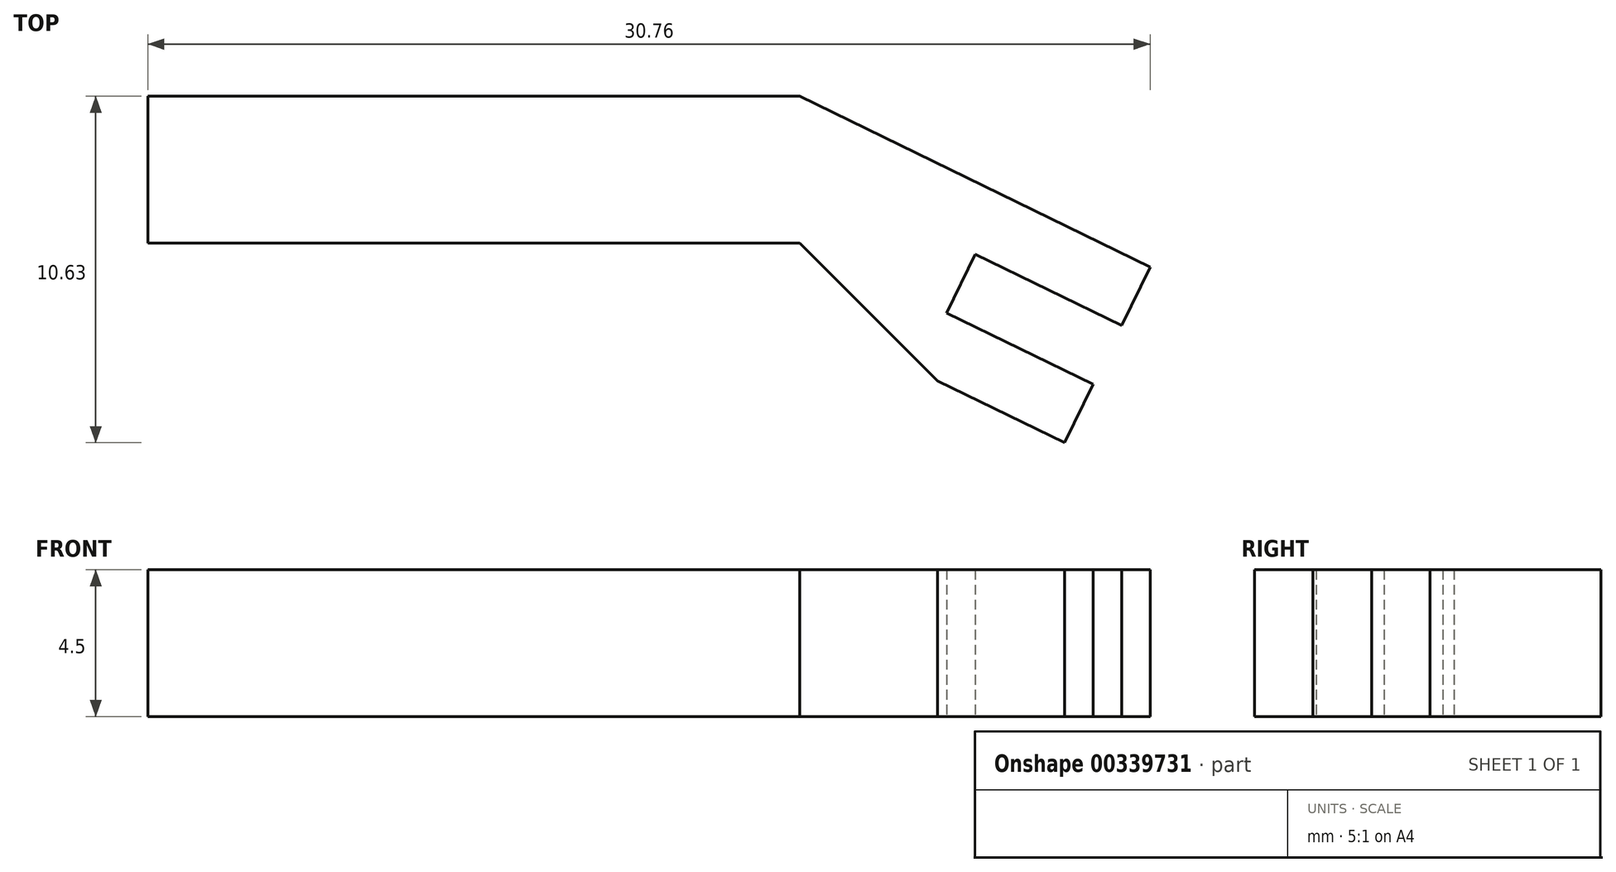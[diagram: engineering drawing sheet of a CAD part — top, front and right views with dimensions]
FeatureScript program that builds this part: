
annotation { "Feature Type Name" : "Feature", "Feature Type Description" : "" }
export const myFeature = defineFeature(function(context is Context, id is Id, definition is map)
    precondition{}
    {
        {
            var Q0;
            Q0=qCreatedBy(makeId("Top.planeOp"),FACE);
            var sketch = newSketch(context, id + "F0", { "sketchPlane" : qUnion([Q0])});
            skLineSegment(sketch, "E0.bottom", {"start": v(10, -2.25) * mm, "end": v(-10, -2.25) * mm});
            skLineSegment(sketch, "E0.top", {"start": v(10, 2.25) * mm, "end": v(-10, 2.25) * mm});
            skLineSegment(sketch, "E0.left", {"start": v(10, -2.25) * mm, "end": v(10, 2.25) * mm});
            skLineSegment(sketch, "E0.right", {"start": v(-10, -2.25) * mm, "end": v(-10, 2.25) * mm});
            skPoint(sketch, "E0.middle", {"position": v(0, 0) * mm});
            skLineSegment(sketch, "E1", {"start": v(10, 2.25) * mm, "end": v(20.76, -2.99) * mm});
            skLineSegment(sketch, "E2", {"start": v(20.76, -2.99) * mm, "end": v(17.48, -9.73) * mm});
            skLineSegment(sketch, "E3", {"start": v(17.48, -9.73) * mm, "end": v(10, -2.25) * mm});
            skPoint(sketch, "E4", {"position": v(19.12, -6.36) * mm});
            skLineSegment(sketch, "E5", {"start": v(19.01, -6.58) * mm, "end": v(14.52, -4.4) * mm});
            skLineSegment(sketch, "E6", {"start": v(14.52, -4.4) * mm, "end": v(15.4, -2.6) * mm});
            skLineSegment(sketch, "E7", {"start": v(15.4, -2.6) * mm, "end": v(19.89, -4.79) * mm});
            skPoint(sketch, "E8", {"position": v(18.14, -8.38) * mm});
            skLineSegment(sketch, "E9", {"start": v(18.14, -8.38) * mm, "end": v(14.23, -6.48) * mm});
            skSolve(sketch);
        }
        {
            var Q0;
            Q0=makeQuery(id+"F0.imprint","IMPRINT",FACE,{"disambiguationData":[TD([[makeQuery(id+"F0.imprint","IMPRINT",EDGE,{"derivedFrom":sQuery(id+"F0.wireOp",EDGE,"E0.bottom")}),-1.0]])]});
            var Q1;
            Q1=makeQuery(id+"F0.imprint","IMPRINT",FACE,{"disambiguationData":[TD([[makeQuery(id+"F0.imprint","IMPRINT",EDGE,{"derivedFrom":sQuery(id+"F0.wireOp",EDGE,"E0.left")}),-1.0]])]});
            extrude(context, id + "F1", {"entities" : qUnion([Q0, Q1]), "depth" : 4.5 * mm});
        }
    });
